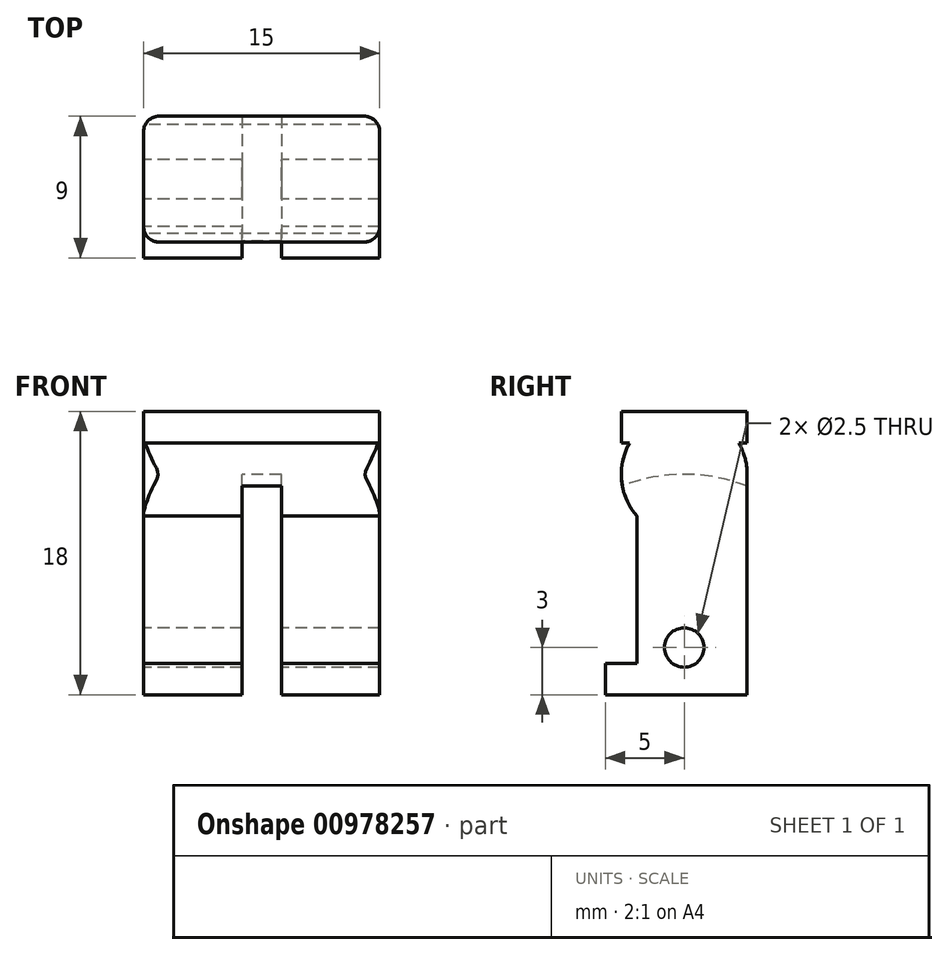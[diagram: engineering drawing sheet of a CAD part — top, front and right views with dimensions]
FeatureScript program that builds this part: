
annotation { "Feature Type Name" : "Feature", "Feature Type Description" : "" }
export const myFeature = defineFeature(function(context is Context, id is Id, definition is map)
    precondition{}
    {
        {
            var Q0;
            Q0=qCreatedBy(makeId("Right.planeOp"),FACE);
            var sketch = newSketch(context, id + "F0", { "sketchPlane" : qUnion([Q0])});
            skLineSegment(sketch, "E0.bottom", {"start": v(4, -1) * mm, "end": v(3.46, -1) * mm});
            skLineSegment(sketch, "E0.top", {"start": v(4, 1) * mm, "end": v(-4, 1) * mm});
            skLineSegment(sketch, "E0.left", {"start": v(4, -1) * mm, "end": v(4, 1) * mm});
            skLineSegment(sketch, "E0.right", {"start": v(-4, -1) * mm, "end": v(-4, 1) * mm});
            skPoint(sketch, "E0.middle", {"position": v(0, 0) * mm});
            skArc(sketch, "E1", {"start": v(-3.46, -1) * mm, "mid": v(-3.98, -3.4) * mm, "end": v(-3, -5.65) * mm});
            skLineSegment(sketch, "E2.left", {"start": v(4, -3) * mm, "end": v(4, -15) * mm});
            skLineSegment(sketch, "E2.right", {"start": v(-3, -5.65) * mm, "end": v(-3, -15) * mm});
            skLineSegment(sketch, "E3.top", {"start": v(4, -17) * mm, "end": v(-5, -17) * mm});
            skLineSegment(sketch, "E3.left", {"start": v(4, -15) * mm, "end": v(4, -17) * mm});
            skLineSegment(sketch, "E3.right", {"start": v(-5, -15) * mm, "end": v(-5, -17) * mm});
            skCircle(sketch, "E4", {"center": v(0, -14) * mm, "radius": 1.25 * mm});
            skLineSegment(sketch, "E5.trimOffspring", {"start": v(-3.46, -1) * mm, "end": v(-4, -1) * mm});
            skArc(sketch, "E6.trimOffspring", {"start": v(4, -3) * mm, "mid": v(3.86, -1.96) * mm, "end": v(3.46, -1) * mm});
            skLineSegment(sketch, "E7.trimOffspring", {"start": v(-3, -15) * mm, "end": v(-5, -15) * mm});
            skSolve(sketch);
        }
        {
            var Q0;
            Q0=qSketchRegion(id+"F0",true);
            extrude(context, id + "F1", {"entities" : qUnion([Q0]), "endBound" : BoundingType.SYMMETRIC, "depth" : 15 * mm, "offsetDistance" : 25.4 * mm});
        }
        {
            var Q0;
            Q0=qCreatedBy(makeId("Right.planeOp"),FACE);
            var sketch = newSketch(context, id + "F2", { "sketchPlane" : qUnion([Q0])});
            skCircle(sketch, "E8", {"center": v(0, -14) * mm, "radius": 11 * mm});
            skSolve(sketch);
        }
        {
            var Q0;
            Q0=qSketchRegion(id+"F2",true);
            extrude(context, id + "F3", {"entities" : qUnion([Q0]), "operationType" : NewBodyOperationType.REMOVE, "endBound" : BoundingType.SYMMETRIC, "depth" : 2.5 * mm, "offsetDistance" : 25.4 * mm});
        }
        {
            var Q0;
            Q0=makeQuery(id+"F1.opExtrude","CAP_EDGE",EDGE,{"disambiguationData":[OSD([sQuery(id+"F0.wireOp",EDGE,"E0.right")])],"isStart":false});
            fillet(context, id + "F4", {"entities" : qUnion([Q0]), "radius" : 1 * mm, "tangentPropagation" : true, "allowEdgeOverflow" : false});
        }
        {
            var Q0;
            Q0=makeQuery(id+"F1.opExtrude","CAP_EDGE",EDGE,{"disambiguationData":[OSD([sQuery(id+"F0.wireOp",EDGE,"E0.left")])],"isStart":false});
            fillet(context, id + "F5", {"entities" : qUnion([Q0]), "radius" : 1 * mm, "tangentPropagation" : true, "allowEdgeOverflow" : false});
        }
        {
            var Q0;
            Q0=makeQuery(id+"F1.opExtrude","CAP_EDGE",EDGE,{"disambiguationData":[OSD([sQuery(id+"F0.wireOp",EDGE,"E0.right")])],"isStart":true});
            fillet(context, id + "F6", {"entities" : qUnion([Q0]), "radius" : 1 * mm, "tangentPropagation" : true, "allowEdgeOverflow" : false});
        }
        {
            var Q0;
            Q0=makeQuery(id+"F1.opExtrude","CAP_EDGE",EDGE,{"disambiguationData":[OSD([sQuery(id+"F0.wireOp",EDGE,"E0.left")])],"isStart":true});
            fillet(context, id + "F7", {"entities" : qUnion([Q0]), "radius" : 1 * mm, "tangentPropagation" : true, "allowEdgeOverflow" : false});
        }
    });
